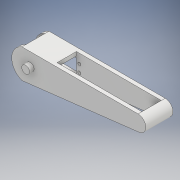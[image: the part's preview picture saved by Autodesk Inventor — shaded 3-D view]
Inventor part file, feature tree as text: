
AUTODESK INVENTOR PART (.ipt)
format: ipt  version: 2018 (Build 220112000, 112)  size: 180,224 bytes
history: native  units: mm
features: extrude x7, sketch x7, plane x1, mirror x1
ambient origin geometry x8: Origin, YZ Plane, XZ Plane, XY Plane, X Axis, Y Axis, Z Axis, Center Point
bodies: Solid1 (feature_tree)
feature tree (16):
  extrude  "Extrusion1"  Depth=20.0mm
  sketch  "Sketch5"  dims[d3=20.0mm d4=5.0mm d5=0.0mm]
  extrude  "Extrusion3"  Depth=5.0mm TaperAngle=0.0deg
  plane  "Work Plane1"
  mirror  "Mirror1"
  extrude  "Extrusion4"  Depth=20.0mm
  extrude  "Extrusion6"  TaperAngle=0.0deg  [1 undecoded]
  extrude  "Extrusion7"  Depth=5.0mm
  extrude  "Extrusion10"  Depth=5.0mm TaperAngle=0.0deg
  extrude  "Extrusion11"  Depth=5.0mm TaperAngle=0.0deg
  sketch  "Sketch1"  dims[d0=150.0mm d1=20.0mm]
  sketch  "Sketch8"  dims[d13=40.3mm d14=20.0mm]
  sketch  "Sketch11"  dims[d15=7.0mm d16=0.0mm]
  sketch  "Sketch14"  dims[d17=5.0mm d18=0.0mm d19=12.5mm]
  sketch  "Sketch17"  dims[d20=5.0mm d21=0.0mm d29=5.0mm d30=0.0mm]
  sketch  "Sketch18"  dims[d31=40.0mm d32=5.0mm d33=0.0mm d38=34.75mm d39=0.0mm d40=6.0mm d41=0.0mm d42=10.0mm]
note: 1 required parameter value undecoded (feature->parameter linkage not recoverable at this tier; creation-order binding heuristic only, values carry confidence <= 0.55)
